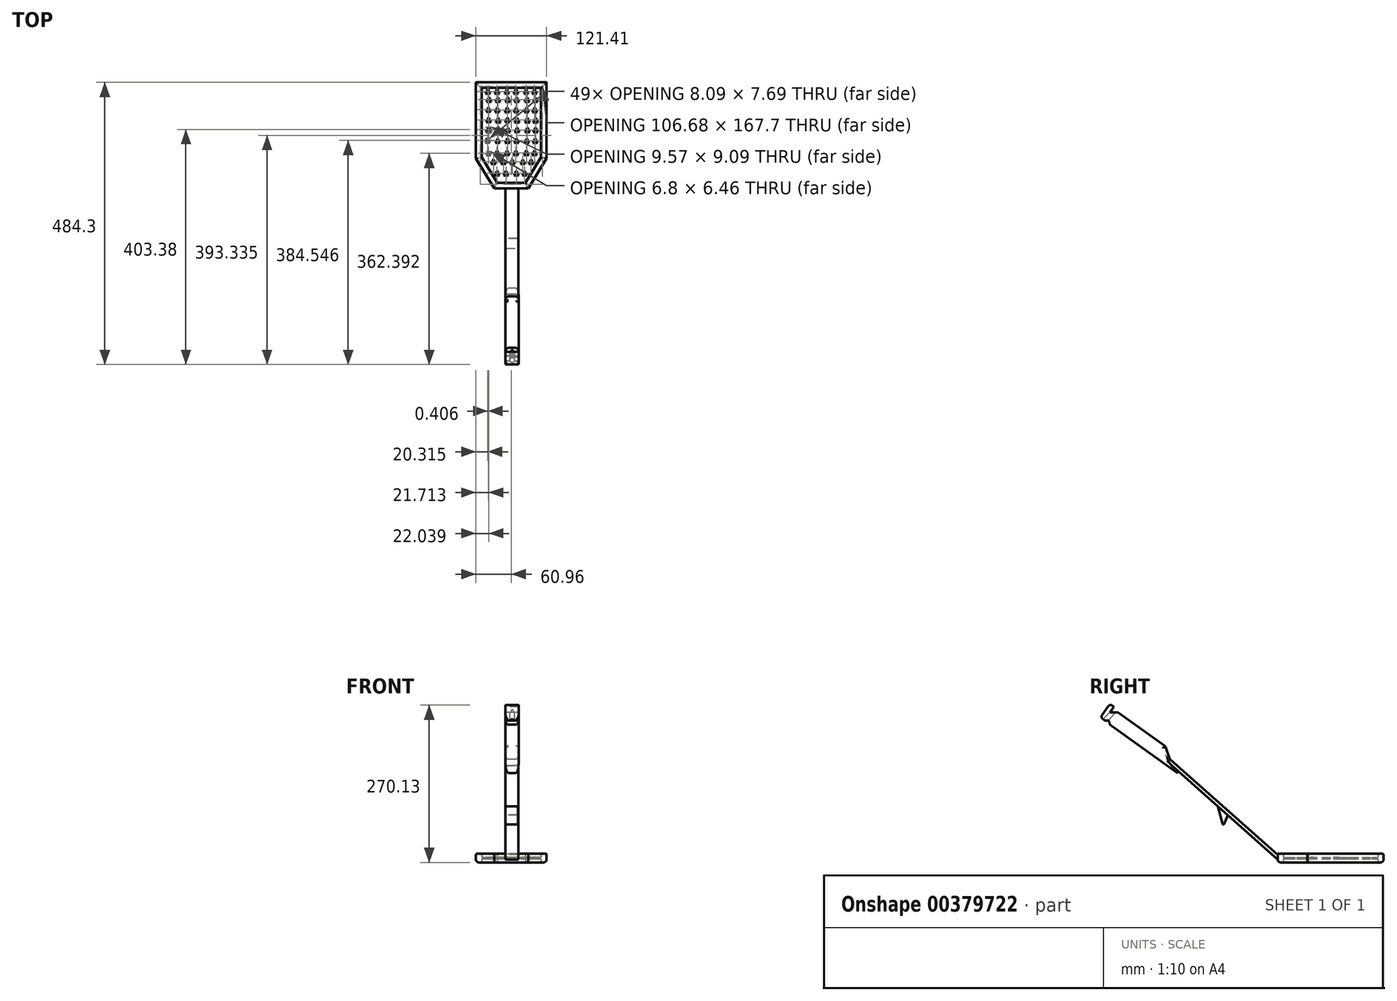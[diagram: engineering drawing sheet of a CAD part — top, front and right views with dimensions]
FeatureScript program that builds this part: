
annotation { "Feature Type Name" : "Feature", "Feature Type Description" : "" }
export const myFeature = defineFeature(function(context is Context, id is Id, definition is map)
    precondition{}
    {
        {
            var Q0;
            Q0=qCreatedBy(makeId("Top.planeOp"),FACE);
            var sketch = newSketch(context, id + "F0", { "sketchPlane" : qUnion([Q0])});
            skLineSegment(sketch, "E0", {"start": v(-14.17, -76.81) * mm, "end": v(34.1, -76.81) * mm});
            skLineSegment(sketch, "E1", {"start": v(-14.17, -76.81) * mm, "end": v(-40.84, -33.58) * mm});
            skLineSegment(sketch, "E2", {"start": v(-40.84, -33.58) * mm, "end": v(-40.84, 85.8) * mm});
            skLineSegment(sketch, "E3", {"start": v(-40.84, 85.8) * mm, "end": v(60.76, 85.8) * mm});
            skLineSegment(sketch, "E4", {"start": v(60.76, 85.8) * mm, "end": v(60.76, -33.58) * mm});
            skLineSegment(sketch, "E5", {"start": v(60.76, -33.58) * mm, "end": v(34.1, -76.81) * mm});
            skLineSegment(sketch, "E6", {"start": v(-51, 95.46) * mm, "end": v(70.41, 95.46) * mm});
            skLineSegment(sketch, "E7", {"start": v(70.41, 95.46) * mm, "end": v(70.41, -35.5) * mm});
            skLineSegment(sketch, "E8", {"start": v(70.41, -35.5) * mm, "end": v(38.97, -86.46) * mm});
            skLineSegment(sketch, "E9", {"start": v(38.97, -86.46) * mm, "end": v(-19.56, -86.46) * mm});
            skLineSegment(sketch, "E10", {"start": v(-19.56, -86.46) * mm, "end": v(-51, -35.5) * mm});
            skLineSegment(sketch, "E11", {"start": v(-51, -35.5) * mm, "end": v(-51, 95.46) * mm});
            skSolve(sketch);
        }
        {
            var Q0;
            Q0=makeQuery(id+"F0.imprint","IMPRINT",FACE,{"disambiguationData":[TD([[makeQuery(id+"F0.imprint","IMPRINT",EDGE,{"derivedFrom":sQuery(id+"F0.wireOp",EDGE,"E0")}),-1.0]])]});
            extrude(context, id + "F1", {"entities" : qUnion([Q0]), "depth" : 7.62 * mm});
        }
        {
            var Q0;
            Q0 = qSketchRegion(id + "F0", true);
            extrude(context, id + "F2", {"entities" : qUnion([Q0]), "operationType" : NewBodyOperationType.ADD, "oppositeDirection" : true, "depth" : 7.62 * mm});
        }
        {
            var Q0;
            Q0=qCreatedBy(makeId("Top.planeOp"),FACE);
            var sketch = newSketch(context, id + "F3", { "sketchPlane" : qUnion([Q0])});
            skLineSegment(sketch, "E12.0", {"start": v(-14.17, -76.81) * mm, "end": v(34.1, -76.81) * mm});
            skLineSegment(sketch, "E12.1", {"start": v(-14.17, -76.81) * mm, "end": v(-40.84, -33.58) * mm});
            skLineSegment(sketch, "E12.2", {"start": v(-40.84, -33.58) * mm, "end": v(-40.84, 85.8) * mm});
            skLineSegment(sketch, "E12.3", {"start": v(-40.84, 85.8) * mm, "end": v(60.76, 85.8) * mm});
            skLineSegment(sketch, "E12.4", {"start": v(60.76, 85.8) * mm, "end": v(60.76, -33.58) * mm});
            skLineSegment(sketch, "E12.5", {"start": v(60.76, -33.58) * mm, "end": v(34.1, -76.81) * mm});
            skLineSegment(sketch, "E12.6", {"start": v(70.41, 95.46) * mm, "end": v(70.41, -35.5) * mm});
            skLineSegment(sketch, "E12.7", {"start": v(70.41, -35.5) * mm, "end": v(38.97, -86.46) * mm});
            skLineSegment(sketch, "E12.8", {"start": v(38.97, -86.46) * mm, "end": v(-19.56, -86.46) * mm});
            skLineSegment(sketch, "E12.9", {"start": v(-19.56, -86.46) * mm, "end": v(-51, -35.5) * mm});
            skLineSegment(sketch, "E13.0", {"start": v(-51, 95.46) * mm, "end": v(70.41, 95.46) * mm});
            skLineSegment(sketch, "E13.1", {"start": v(-51, -35.5) * mm, "end": v(-51, 95.46) * mm});
            skLineSegment(sketch, "E13.6", {"start": v(-51, -35.5) * mm, "end": v(-51, 95.46) * mm});
            skLineSegment(sketch, "E13.9", {"start": v(-51, 95.46) * mm, "end": v(70.41, 95.46) * mm});
            skSolve(sketch);
        }
        {
            var Q0;
            Q0=qCreatedBy(makeId("Top.planeOp"),FACE);
            var sketch = newSketch(context, id + "F4", { "sketchPlane" : qUnion([Q0])});
            skLineSegment(sketch, "E14.0", {"start": v(-51, 95.46) * mm, "end": v(70.41, 95.46) * mm});
            skLineSegment(sketch, "E14.1", {"start": v(-51, 95.46) * mm, "end": v(70.41, 95.46) * mm});
            skLineSegment(sketch, "E15.0", {"start": v(70.41, 95.46) * mm, "end": v(70.41, -35.5) * mm});
            skLineSegment(sketch, "E15.1", {"start": v(70.41, 95.46) * mm, "end": v(70.41, -35.5) * mm});
            skLineSegment(sketch, "E16.0", {"start": v(-51, -35.5) * mm, "end": v(-51, 95.46) * mm});
            skLineSegment(sketch, "E16.1", {"start": v(-51, -35.5) * mm, "end": v(-51, 95.46) * mm});
            skPoint(sketch, "E17.0", {"position": v(-19.56, -86.46) * mm});
            skLineSegment(sketch, "E18.0", {"start": v(38.97, -86.46) * mm, "end": v(-19.56, -86.46) * mm});
            skLineSegment(sketch, "E18.1", {"start": v(38.97, -86.46) * mm, "end": v(-19.56, -86.46) * mm});
            skLineSegment(sketch, "E19", {"start": v(-51, -35.5) * mm, "end": v(-19.56, -86.46) * mm});
            skLineSegment(sketch, "E20", {"start": v(70.41, -35.5) * mm, "end": v(38.97, -86.46) * mm});
            skLineSegment(sketch, "E21.MirrorCS", {"start": v(-18.83, 76.12) * mm, "end": v(-14.78, 83.8) * mm});
            skLineSegment(sketch, "E22.MirrorCS", {"start": v(-14.78, 83.8) * mm, "end": v(-10.73, 76.12) * mm});
            skLineSegment(sketch, "E23.MirrorCS", {"start": v(-10.73, 76.12) * mm, "end": v(-18.83, 76.12) * mm});
            skLineSegment(sketch, "E24.MirrorCS", {"start": v(6.26, 76.12) * mm, "end": v(2.22, 83.8) * mm});
            skLineSegment(sketch, "E25.MirrorCS", {"start": v(13.54, 76.12) * mm, "end": v(17.6, 83.8) * mm});
            skLineSegment(sketch, "E26.MirrorCS", {"start": v(17.6, 83.8) * mm, "end": v(21.64, 76.12) * mm});
            skLineSegment(sketch, "E27.MirrorCS", {"start": v(-1.83, 76.12) * mm, "end": v(6.26, 76.12) * mm});
            skLineSegment(sketch, "E28.MirrorCS", {"start": v(2.22, 83.8) * mm, "end": v(-1.83, 76.12) * mm});
            skLineSegment(sketch, "E29.MirrorCS", {"start": v(21.64, 76.12) * mm, "end": v(13.54, 76.12) * mm});
            skLineSegment(sketch, "E30.MirrorCS", {"start": v(45.52, 76.12) * mm, "end": v(49.56, 83.8) * mm});
            skLineSegment(sketch, "E31.MirrorCS", {"start": v(35.4, 83.8) * mm, "end": v(31.35, 76.12) * mm});
            skLineSegment(sketch, "E32.MirrorCS", {"start": v(31.35, 76.12) * mm, "end": v(39.44, 76.12) * mm});
            skLineSegment(sketch, "E33.MirrorCS", {"start": v(53.6, 76.12) * mm, "end": v(45.52, 76.12) * mm});
            skLineSegment(sketch, "E34.MirrorCS", {"start": v(39.44, 76.12) * mm, "end": v(35.4, 83.8) * mm});
            skLineSegment(sketch, "E35.MirrorCS", {"start": v(49.56, 83.8) * mm, "end": v(53.6, 76.12) * mm});
            skLineSegment(sketch, "E36.MirrorCS", {"start": v(-17.21, 61.78) * mm, "end": v(-13.17, 69.47) * mm});
            skLineSegment(sketch, "E37.MirrorCS", {"start": v(-13.17, 69.47) * mm, "end": v(-9.12, 61.78) * mm});
            skLineSegment(sketch, "E38.MirrorCS", {"start": v(-9.12, 61.78) * mm, "end": v(-17.21, 61.78) * mm});
            skLineSegment(sketch, "E39.MirrorCS", {"start": v(7.87, 61.78) * mm, "end": v(3.83, 69.47) * mm});
            skLineSegment(sketch, "E40.MirrorCS", {"start": v(15.16, 61.78) * mm, "end": v(19.2, 69.47) * mm});
            skLineSegment(sketch, "E41.MirrorCS", {"start": v(19.2, 69.47) * mm, "end": v(23.25, 61.78) * mm});
            skLineSegment(sketch, "E42.MirrorCS", {"start": v(-0.22, 61.78) * mm, "end": v(7.87, 61.78) * mm});
            skLineSegment(sketch, "E43.MirrorCS", {"start": v(3.83, 69.47) * mm, "end": v(-0.22, 61.78) * mm});
            skLineSegment(sketch, "E44.MirrorCS", {"start": v(23.25, 61.78) * mm, "end": v(15.16, 61.78) * mm});
            skLineSegment(sketch, "E45.MirrorCS", {"start": v(47.13, 61.78) * mm, "end": v(51.17, 69.47) * mm});
            skLineSegment(sketch, "E46.MirrorCS", {"start": v(37, 69.47) * mm, "end": v(32.96, 61.78) * mm});
            skLineSegment(sketch, "E47.MirrorCS", {"start": v(32.96, 61.78) * mm, "end": v(41.05, 61.78) * mm});
            skLineSegment(sketch, "E48.MirrorCS", {"start": v(55.22, 61.78) * mm, "end": v(47.13, 61.78) * mm});
            skLineSegment(sketch, "E49.MirrorCS", {"start": v(41.05, 61.78) * mm, "end": v(37, 69.47) * mm});
            skLineSegment(sketch, "E50.MirrorCS", {"start": v(51.17, 69.47) * mm, "end": v(55.22, 61.78) * mm});
            skLineSegment(sketch, "E51.MirrorCS", {"start": v(-18.36, 44.38) * mm, "end": v(-14.28, 52.14) * mm});
            skLineSegment(sketch, "E52.MirrorCS", {"start": v(-14.28, 52.14) * mm, "end": v(-10.23, 44.46) * mm});
            skLineSegment(sketch, "E53.MirrorCS", {"start": v(-18.33, 44.46) * mm, "end": v(-14.28, 52.14) * mm});
            skLineSegment(sketch, "E54.MirrorCS", {"start": v(-10.23, 44.46) * mm, "end": v(-18.33, 44.46) * mm});
            skLineSegment(sketch, "E55.MirrorCS", {"start": v(6.76, 44.46) * mm, "end": v(2.72, 52.14) * mm});
            skLineSegment(sketch, "E56.MirrorCS", {"start": v(14.05, 44.46) * mm, "end": v(18.1, 52.14) * mm});
            skLineSegment(sketch, "E57.MirrorCS", {"start": v(18.1, 52.14) * mm, "end": v(22.14, 44.46) * mm});
            skLineSegment(sketch, "E58.MirrorCS", {"start": v(-1.33, 44.46) * mm, "end": v(6.76, 44.46) * mm});
            skLineSegment(sketch, "E59.MirrorCS", {"start": v(2.72, 52.14) * mm, "end": v(-1.33, 44.46) * mm});
            skLineSegment(sketch, "E60.MirrorCS", {"start": v(22.14, 44.46) * mm, "end": v(14.05, 44.46) * mm});
            skLineSegment(sketch, "E61.MirrorCS", {"start": v(46.02, 44.46) * mm, "end": v(50.06, 52.14) * mm});
            skLineSegment(sketch, "E62.MirrorCS", {"start": v(35.9, 52.14) * mm, "end": v(31.85, 44.46) * mm});
            skLineSegment(sketch, "E63.MirrorCS", {"start": v(31.85, 44.46) * mm, "end": v(39.94, 44.46) * mm});
            skLineSegment(sketch, "E64.MirrorCS", {"start": v(54.11, 44.46) * mm, "end": v(46.02, 44.46) * mm});
            skLineSegment(sketch, "E65.MirrorCS", {"start": v(39.94, 44.46) * mm, "end": v(35.9, 52.14) * mm});
            skLineSegment(sketch, "E66.MirrorCS", {"start": v(50.06, 52.14) * mm, "end": v(54.11, 44.46) * mm});
            skLineSegment(sketch, "E67.MirrorCS", {"start": v(-12.67, 34.42) * mm, "end": v(-8.62, 26.73) * mm});
            skLineSegment(sketch, "E68.MirrorCS", {"start": v(-16.71, 26.73) * mm, "end": v(-12.67, 34.42) * mm});
            skLineSegment(sketch, "E69.MirrorCS", {"start": v(-8.62, 26.73) * mm, "end": v(-16.71, 26.73) * mm});
            skLineSegment(sketch, "E70.MirrorCS", {"start": v(15.66, 26.73) * mm, "end": v(19.7, 34.42) * mm});
            skLineSegment(sketch, "E71.MirrorCS", {"start": v(19.7, 34.42) * mm, "end": v(23.75, 26.73) * mm});
            skLineSegment(sketch, "E72.MirrorCS", {"start": v(23.75, 26.73) * mm, "end": v(15.66, 26.73) * mm});
            skLineSegment(sketch, "E73.MirrorCS", {"start": v(47.63, 26.73) * mm, "end": v(51.68, 34.42) * mm});
            skLineSegment(sketch, "E74.MirrorCS", {"start": v(37.5, 34.42) * mm, "end": v(33.46, 26.73) * mm});
            skLineSegment(sketch, "E75.MirrorCS", {"start": v(33.46, 26.73) * mm, "end": v(41.55, 26.73) * mm});
            skLineSegment(sketch, "E76.MirrorCS", {"start": v(55.72, 26.73) * mm, "end": v(47.63, 26.73) * mm});
            skLineSegment(sketch, "E77.MirrorCS", {"start": v(41.55, 26.73) * mm, "end": v(37.5, 34.42) * mm});
            skLineSegment(sketch, "E78.MirrorCS", {"start": v(51.68, 34.42) * mm, "end": v(55.72, 26.73) * mm});
            skLineSegment(sketch, "E79", {"start": v(-33.75, 10) * mm, "end": v(-24.18, 10) * mm});
            skLineSegment(sketch, "E80", {"start": v(-24.18, 10) * mm, "end": v(-28.96, 19.09) * mm});
            skLineSegment(sketch, "E81", {"start": v(-28.96, 19.09) * mm, "end": v(-33.75, 10) * mm});
            skLineSegment(sketch, "E82.MirrorCS", {"start": v(-16.8, 9.8) * mm, "end": v(-12.75, 17.5) * mm});
            skLineSegment(sketch, "E83.MirrorCS", {"start": v(-12.75, 17.5) * mm, "end": v(-8.7, 9.8) * mm});
            skLineSegment(sketch, "E84.MirrorCS", {"start": v(-8.7, 9.8) * mm, "end": v(-16.8, 9.8) * mm});
            skLineSegment(sketch, "E85.MirrorCS", {"start": v(8.3, 9.8) * mm, "end": v(4.25, 17.5) * mm});
            skLineSegment(sketch, "E86.MirrorCS", {"start": v(15.58, 9.8) * mm, "end": v(19.62, 17.5) * mm});
            skLineSegment(sketch, "E87.MirrorCS", {"start": v(19.62, 17.5) * mm, "end": v(23.67, 9.8) * mm});
            skLineSegment(sketch, "E88.MirrorCS", {"start": v(0.2, 9.8) * mm, "end": v(8.3, 9.8) * mm});
            skLineSegment(sketch, "E89.MirrorCS", {"start": v(4.25, 17.5) * mm, "end": v(0.2, 9.8) * mm});
            skLineSegment(sketch, "E90.MirrorCS", {"start": v(23.67, 9.8) * mm, "end": v(15.58, 9.8) * mm});
            skLineSegment(sketch, "E91.MirrorCS", {"start": v(47.55, 9.8) * mm, "end": v(51.6, 17.5) * mm});
            skLineSegment(sketch, "E92.MirrorCS", {"start": v(37.43, 17.5) * mm, "end": v(33.38, 9.8) * mm});
            skLineSegment(sketch, "E93.MirrorCS", {"start": v(33.38, 9.8) * mm, "end": v(41.47, 9.8) * mm});
            skLineSegment(sketch, "E94.MirrorCS", {"start": v(55.64, 9.8) * mm, "end": v(47.55, 9.8) * mm});
            skLineSegment(sketch, "E95.MirrorCS", {"start": v(41.47, 9.8) * mm, "end": v(37.43, 17.5) * mm});
            skLineSegment(sketch, "E96.MirrorCS", {"start": v(51.6, 17.5) * mm, "end": v(55.64, 9.8) * mm});
            skLineSegment(sketch, "E97.MirrorCS", {"start": v(-17.6, -8.32) * mm, "end": v(-13.55, -0.63) * mm});
            skLineSegment(sketch, "E98.MirrorCS", {"start": v(-13.55, -0.63) * mm, "end": v(-9.5, -8.32) * mm});
            skLineSegment(sketch, "E99.MirrorCS", {"start": v(-9.5, -8.32) * mm, "end": v(-17.6, -8.32) * mm});
            skLineSegment(sketch, "E100.MirrorCS", {"start": v(7.49, -8.32) * mm, "end": v(3.44, -0.63) * mm});
            skLineSegment(sketch, "E101.MirrorCS", {"start": v(14.77, -8.32) * mm, "end": v(18.82, -0.63) * mm});
            skLineSegment(sketch, "E102.MirrorCS", {"start": v(18.82, -0.63) * mm, "end": v(22.86, -8.32) * mm});
            skLineSegment(sketch, "E103.MirrorCS", {"start": v(-0.6, -8.32) * mm, "end": v(7.49, -8.32) * mm});
            skLineSegment(sketch, "E104.MirrorCS", {"start": v(3.44, -0.63) * mm, "end": v(-0.6, -8.32) * mm});
            skLineSegment(sketch, "E105.MirrorCS", {"start": v(22.86, -8.32) * mm, "end": v(14.77, -8.32) * mm});
            skLineSegment(sketch, "E106.MirrorCS", {"start": v(46.74, -8.32) * mm, "end": v(50.79, -0.63) * mm});
            skLineSegment(sketch, "E107.MirrorCS", {"start": v(36.62, -0.63) * mm, "end": v(32.58, -8.32) * mm});
            skLineSegment(sketch, "E108.MirrorCS", {"start": v(32.58, -8.32) * mm, "end": v(40.67, -8.32) * mm});
            skLineSegment(sketch, "E109.MirrorCS", {"start": v(54.84, -8.32) * mm, "end": v(46.74, -8.32) * mm});
            skLineSegment(sketch, "E110.MirrorCS", {"start": v(40.67, -8.32) * mm, "end": v(36.62, -0.63) * mm});
            skLineSegment(sketch, "E111.MirrorCS", {"start": v(50.79, -0.63) * mm, "end": v(54.84, -8.32) * mm});
            skLineSegment(sketch, "E112", {"start": v(-32.69, -29.68) * mm, "end": v(-25.89, -29.68) * mm});
            skLineSegment(sketch, "E113", {"start": v(-25.89, -29.68) * mm, "end": v(-29.29, -23.22) * mm});
            skLineSegment(sketch, "E114", {"start": v(-29.29, -23.22) * mm, "end": v(-32.69, -29.68) * mm});
            skLineSegment(sketch, "E115.MirrorCS", {"start": v(-18.6, -29.68) * mm, "end": v(-14.56, -21.99) * mm});
            skLineSegment(sketch, "E116.MirrorCS", {"start": v(-14.56, -21.99) * mm, "end": v(-10.51, -29.68) * mm});
            skLineSegment(sketch, "E117.MirrorCS", {"start": v(-10.51, -29.68) * mm, "end": v(-18.6, -29.68) * mm});
            skLineSegment(sketch, "E118.MirrorCS", {"start": v(6.48, -29.68) * mm, "end": v(2.44, -21.99) * mm});
            skLineSegment(sketch, "E119.MirrorCS", {"start": v(13.77, -29.68) * mm, "end": v(17.81, -21.99) * mm});
            skLineSegment(sketch, "E120.MirrorCS", {"start": v(17.81, -21.99) * mm, "end": v(21.86, -29.68) * mm});
            skLineSegment(sketch, "E121.MirrorCS", {"start": v(-1.61, -29.68) * mm, "end": v(6.48, -29.68) * mm});
            skLineSegment(sketch, "E122.MirrorCS", {"start": v(2.44, -21.99) * mm, "end": v(-1.61, -29.68) * mm});
            skLineSegment(sketch, "E123.MirrorCS", {"start": v(21.86, -29.68) * mm, "end": v(13.77, -29.68) * mm});
            skLineSegment(sketch, "E124.MirrorCS", {"start": v(45.74, -29.68) * mm, "end": v(49.78, -21.99) * mm});
            skLineSegment(sketch, "E125.MirrorCS", {"start": v(35.62, -21.99) * mm, "end": v(31.57, -29.68) * mm});
            skLineSegment(sketch, "E126.MirrorCS", {"start": v(31.57, -29.68) * mm, "end": v(39.66, -29.68) * mm});
            skLineSegment(sketch, "E127.MirrorCS", {"start": v(53.83, -29.68) * mm, "end": v(45.74, -29.68) * mm});
            skLineSegment(sketch, "E128.MirrorCS", {"start": v(39.66, -29.68) * mm, "end": v(35.62, -21.99) * mm});
            skLineSegment(sketch, "E129.MirrorCS", {"start": v(49.78, -21.99) * mm, "end": v(53.83, -29.68) * mm});
            skLineSegment(sketch, "E130.MirrorCS", {"start": v(-24.7, -44.99) * mm, "end": v(-20.66, -37.3) * mm});
            skLineSegment(sketch, "E131.MirrorCS", {"start": v(-20.66, -37.3) * mm, "end": v(-16.6, -44.99) * mm});
            skLineSegment(sketch, "E132.MirrorCS", {"start": v(-16.6, -44.99) * mm, "end": v(-24.7, -44.99) * mm});
            skLineSegment(sketch, "E133.MirrorCS", {"start": v(0.39, -44.99) * mm, "end": v(-3.66, -37.3) * mm});
            skLineSegment(sketch, "E134.MirrorCS", {"start": v(7.67, -44.99) * mm, "end": v(11.72, -37.3) * mm});
            skLineSegment(sketch, "E135.MirrorCS", {"start": v(11.72, -37.3) * mm, "end": v(15.76, -44.99) * mm});
            skLineSegment(sketch, "E136.MirrorCS", {"start": v(-7.7, -44.99) * mm, "end": v(0.39, -44.99) * mm});
            skLineSegment(sketch, "E137.MirrorCS", {"start": v(-3.66, -37.3) * mm, "end": v(-7.7, -44.99) * mm});
            skLineSegment(sketch, "E138.MirrorCS", {"start": v(15.76, -44.99) * mm, "end": v(7.67, -44.99) * mm});
            skLineSegment(sketch, "E139.MirrorCS", {"start": v(39.64, -44.99) * mm, "end": v(43.69, -37.3) * mm});
            skLineSegment(sketch, "E140.MirrorCS", {"start": v(29.52, -37.3) * mm, "end": v(25.47, -44.99) * mm});
            skLineSegment(sketch, "E141.MirrorCS", {"start": v(25.47, -44.99) * mm, "end": v(33.57, -44.99) * mm});
            skLineSegment(sketch, "E142.MirrorCS", {"start": v(47.73, -44.99) * mm, "end": v(39.64, -44.99) * mm});
            skLineSegment(sketch, "E143.MirrorCS", {"start": v(33.57, -44.99) * mm, "end": v(29.52, -37.3) * mm});
            skLineSegment(sketch, "E144.MirrorCS", {"start": v(43.69, -37.3) * mm, "end": v(47.73, -44.99) * mm});
            skLineSegment(sketch, "E145.MirrorCS", {"start": v(-10.54, -64.32) * mm, "end": v(-14.58, -56.64) * mm});
            skLineSegment(sketch, "E146.MirrorCS", {"start": v(-3.25, -64.32) * mm, "end": v(0.8, -56.64) * mm});
            skLineSegment(sketch, "E147.MirrorCS", {"start": v(0.8, -56.64) * mm, "end": v(4.84, -64.32) * mm});
            skLineSegment(sketch, "E148.MirrorCS", {"start": v(-18.63, -64.32) * mm, "end": v(-10.54, -64.32) * mm});
            skLineSegment(sketch, "E149.MirrorCS", {"start": v(-14.58, -56.64) * mm, "end": v(-18.63, -64.32) * mm});
            skLineSegment(sketch, "E150.MirrorCS", {"start": v(4.84, -64.32) * mm, "end": v(-3.25, -64.32) * mm});
            skLineSegment(sketch, "E151.MirrorCS", {"start": v(28.72, -64.32) * mm, "end": v(32.77, -56.64) * mm});
            skLineSegment(sketch, "E152.MirrorCS", {"start": v(18.6, -56.64) * mm, "end": v(14.55, -64.32) * mm});
            skLineSegment(sketch, "E153.MirrorCS", {"start": v(14.55, -64.32) * mm, "end": v(22.64, -64.32) * mm});
            skLineSegment(sketch, "E154.MirrorCS", {"start": v(36.81, -64.32) * mm, "end": v(28.72, -64.32) * mm});
            skLineSegment(sketch, "E155.MirrorCS", {"start": v(22.64, -64.32) * mm, "end": v(18.6, -56.64) * mm});
            skLineSegment(sketch, "E156.MirrorCS", {"start": v(32.77, -56.64) * mm, "end": v(36.81, -64.32) * mm});
            skLineSegment(sketch, "E157.MirrorCS", {"start": v(-34.33, 75.74) * mm, "end": v(-30.28, 83.43) * mm});
            skLineSegment(sketch, "E158.MirrorCS", {"start": v(-30.28, 83.43) * mm, "end": v(-26.23, 75.74) * mm});
            skLineSegment(sketch, "E159.MirrorCS", {"start": v(-26.23, 75.74) * mm, "end": v(-34.33, 75.74) * mm});
            skLineSegment(sketch, "E160.MirrorCS", {"start": v(-32.71, 62.05) * mm, "end": v(-28.67, 69.73) * mm});
            skLineSegment(sketch, "E161.MirrorCS", {"start": v(-28.67, 69.73) * mm, "end": v(-24.62, 62.05) * mm});
            skLineSegment(sketch, "E162.MirrorCS", {"start": v(-24.62, 62.05) * mm, "end": v(-32.71, 62.05) * mm});
            skLineSegment(sketch, "E163.MirrorCS", {"start": v(-33.52, 44.72) * mm, "end": v(-29.47, 52.4) * mm});
            skLineSegment(sketch, "E164.MirrorCS", {"start": v(-29.47, 52.4) * mm, "end": v(-25.43, 44.72) * mm});
            skLineSegment(sketch, "E165.MirrorCS", {"start": v(-25.43, 44.72) * mm, "end": v(-33.52, 44.72) * mm});
            skLineSegment(sketch, "E166.MirrorCS", {"start": v(-33.12, 26.96) * mm, "end": v(-29.07, 34.65) * mm});
            skLineSegment(sketch, "E167.MirrorCS", {"start": v(-29.07, 34.65) * mm, "end": v(-25.02, 26.96) * mm});
            skLineSegment(sketch, "E168.MirrorCS", {"start": v(-25.02, 26.96) * mm, "end": v(-33.12, 26.96) * mm});
            skLineSegment(sketch, "E169.MirrorCS", {"start": v(-34.73, -8.14) * mm, "end": v(-30.69, -0.45) * mm});
            skLineSegment(sketch, "E170.MirrorCS", {"start": v(-30.69, -0.45) * mm, "end": v(-26.64, -8.14) * mm});
            skLineSegment(sketch, "E171.MirrorCS", {"start": v(-26.64, -8.14) * mm, "end": v(-34.73, -8.14) * mm});
            skLineSegment(sketch, "E172.MirrorCS", {"start": v(-0.87, 27) * mm, "end": v(3.17, 34.7) * mm});
            skLineSegment(sketch, "E173.MirrorCS", {"start": v(3.17, 34.7) * mm, "end": v(7.22, 27) * mm});
            skLineSegment(sketch, "E174.MirrorCS", {"start": v(7.22, 27) * mm, "end": v(-0.87, 27) * mm});
            skSolve(sketch);
        }
        {
            var Q0;
            Q0=makeQuery(id+"F1.opExtrude","CAP_EDGE",EDGE,{"disambiguationData":[OSD([sQuery(id+"F0.wireOp",EDGE,"E5")])],"isStart":false});
            var Q1;
            Q1=makeQuery(id+"F1.opExtrude","CAP_EDGE",EDGE,{"disambiguationData":[OSD([sQuery(id+"F0.wireOp",EDGE,"E0")])],"isStart":false});
            var Q2;
            Q2=makeQuery(id+"F1.opExtrude","CAP_EDGE",EDGE,{"disambiguationData":[OSD([sQuery(id+"F0.wireOp",EDGE,"E1")])],"isStart":false});
            var Q3;
            Q3=makeQuery(id+"F1.opExtrude","CAP_EDGE",EDGE,{"disambiguationData":[OSD([sQuery(id+"F0.wireOp",EDGE,"E2")])],"isStart":false});
            var Q4;
            Q4=makeQuery(id+"F1.opExtrude","CAP_EDGE",EDGE,{"disambiguationData":[OSD([sQuery(id+"F0.wireOp",EDGE,"E3")])],"isStart":false});
            var Q5;
            Q5=makeQuery(id+"F1.opExtrude","CAP_EDGE",EDGE,{"disambiguationData":[OSD([sQuery(id+"F0.wireOp",EDGE,"E4")])],"isStart":false});
            var Q6;
            Q6=makeQuery(id+"F1.opExtrude","CAP_EDGE",EDGE,{"disambiguationData":[OSD([sQuery(id+"F0.wireOp",EDGE,"E8")])],"isStart":false});
            var Q7;
            Q7=makeQuery(id+"F1.opExtrude","CAP_EDGE",EDGE,{"disambiguationData":[OSD([sQuery(id+"F0.wireOp",EDGE,"E9")])],"isStart":false});
            var Q8;
            Q8=makeQuery(id+"F1.opExtrude","CAP_EDGE",EDGE,{"disambiguationData":[OSD([sQuery(id+"F0.wireOp",EDGE,"E10")])],"isStart":false});
            var Q9;
            Q9=makeQuery(id+"F1.opExtrude","CAP_EDGE",EDGE,{"disambiguationData":[OSD([sQuery(id+"F0.wireOp",EDGE,"E11")])],"isStart":false});
            var Q10;
            Q10=makeQuery(id+"F1.opExtrude","CAP_EDGE",EDGE,{"disambiguationData":[OSD([sQuery(id+"F0.wireOp",EDGE,"E7")])],"isStart":false});
            var Q11;
            Q11=makeQuery(id+"F1.opExtrude","CAP_EDGE",EDGE,{"disambiguationData":[OSD([sQuery(id+"F0.wireOp",EDGE,"E6")])],"isStart":false});
            var Q12;
            Q12=makeQuery(id+"F2.opExtrude","CAP_EDGE",EDGE,{"disambiguationData":[OSD([sQuery(id+"F0.wireOp",EDGE,"E5")])],"isStart":false});
            var Q13;
            Q13=makeQuery(id+"F2.opExtrude","CAP_EDGE",EDGE,{"disambiguationData":[OSD([sQuery(id+"F0.wireOp",EDGE,"E0")])],"isStart":false});
            var Q14;
            Q14=makeQuery(id+"F2.opExtrude","CAP_EDGE",EDGE,{"disambiguationData":[OSD([sQuery(id+"F0.wireOp",EDGE,"E1")])],"isStart":false});
            var Q15;
            Q15=makeQuery(id+"F2.opExtrude","CAP_EDGE",EDGE,{"disambiguationData":[OSD([sQuery(id+"F0.wireOp",EDGE,"E2")])],"isStart":false});
            var Q16;
            Q16=makeQuery(id+"F2.opExtrude","CAP_EDGE",EDGE,{"disambiguationData":[OSD([sQuery(id+"F0.wireOp",EDGE,"E3")])],"isStart":false});
            var Q17;
            Q17=makeQuery(id+"F2.opExtrude","CAP_EDGE",EDGE,{"disambiguationData":[OSD([sQuery(id+"F0.wireOp",EDGE,"E4")])],"isStart":false});
            fillet(context, id + "F5", {"entities" : qUnion([Q0, Q1, Q2, Q3, Q4, Q5, Q6, Q7, Q8, Q9, Q10, Q11, Q12, Q13, Q14, Q15, Q16, Q17]), "radius" : 2.54 * mm, "tangentPropagation" : true, "allowEdgeOverflow" : false});
        }
        {
            var Q0;
            Q0=makeQuery(id+"F2.opExtrude","CAP_EDGE",EDGE,{"disambiguationData":[OSD([sQuery(id+"F0.wireOp",EDGE,"E7")])],"isStart":false});
            var Q1;
            Q1=makeQuery(id+"F2.opExtrude","CAP_EDGE",EDGE,{"disambiguationData":[OSD([sQuery(id+"F0.wireOp",EDGE,"E6")])],"isStart":false});
            var Q2;
            Q2=makeQuery(id+"F2.opExtrude","CAP_EDGE",EDGE,{"disambiguationData":[OSD([sQuery(id+"F0.wireOp",EDGE,"E11")])],"isStart":false});
            var Q3;
            Q3=makeQuery(id+"F2.opExtrude","CAP_EDGE",EDGE,{"disambiguationData":[OSD([sQuery(id+"F0.wireOp",EDGE,"E10")])],"isStart":false});
            var Q4;
            Q4=makeQuery(id+"F2.opExtrude","CAP_EDGE",EDGE,{"disambiguationData":[OSD([sQuery(id+"F0.wireOp",EDGE,"E9")])],"isStart":false});
            var Q5;
            Q5=makeQuery(id+"F2.opExtrude","CAP_EDGE",EDGE,{"disambiguationData":[OSD([sQuery(id+"F0.wireOp",EDGE,"E8")])],"isStart":false});
            fillet(context, id + "F6", {"entities" : qUnion([Q0, Q1, Q2, Q3, Q4, Q5]), "radius" : 5.08 * mm, "tangentPropagation" : true, "allowEdgeOverflow" : false});
        }
        {
            var Q0;
            Q0 = qSketchRegion(id + "F4", true);
            extrude(context, id + "F7", {"entities" : qUnion([Q0]), "operationType" : NewBodyOperationType.ADD, "endBound" : BoundingType.SYMMETRIC, "oppositeDirection" : true, "depth" : 2.54 * mm});
        }
        {
            var Q0;
            Q0=qCreatedBy(makeId("Right.planeOp"),FACE);
            var sketch = newSketch(context, id + "F8", { "sketchPlane" : qUnion([Q0])});
            skLineSegment(sketch, "E175", {"start": v(-86.15, 5) * mm, "end": v(-352.18, 240.96) * mm});
            skLineSegment(sketch, "E176", {"start": v(-86.54, -2.51) * mm, "end": v(-351.67, 232.64) * mm});
            skLineSegment(sketch, "E177", {"start": v(-351.67, 232.64) * mm, "end": v(-356.05, 236.58) * mm});
            skLineSegment(sketch, "E178", {"start": v(-356.05, 236.58) * mm, "end": v(-352.18, 240.96) * mm});
            skLineSegment(sketch, "E179", {"start": v(-86.15, 5) * mm, "end": v(-86.54, -2.51) * mm});
            skSolve(sketch);
        }
        {
            var Q0;
            Q0=makeQuery(id+"F8.imprint","IMPRINT",FACE,{"disambiguationData":[TD([[makeQuery(id+"F8.imprint","IMPRINT",EDGE,{"derivedFrom":sQuery(id+"F8.wireOp",EDGE,"E175")}),1.0]])]});
            extrude(context, id + "F9", {"entities" : qUnion([Q0]), "operationType" : NewBodyOperationType.ADD, "depth" : 21.84 * mm});
        }
        {
            var Q0;
            Q0=qCreatedBy(makeId("Right.planeOp"),FACE);
            var sketch = newSketch(context, id + "F10", { "sketchPlane" : qUnion([Q0])});
            skLineSegment(sketch, "E180", {"start": v(-268.32, 158.61) * mm, "end": v(-258.08, 146.04) * mm});
            skLineSegment(sketch, "E181", {"start": v(-258.08, 146.04) * mm, "end": v(-374.2, 229.1) * mm});
            skLineSegment(sketch, "E182", {"start": v(-374.2, 229.1) * mm, "end": v(-376.53, 236.11) * mm});
            skLineSegment(sketch, "E183", {"start": v(-376.53, 236.11) * mm, "end": v(-383.26, 236.11) * mm});
            skLineSegment(sketch, "E184", {"start": v(-383.26, 236.11) * mm, "end": v(-390.86, 241.67) * mm});
            skLineSegment(sketch, "E185", {"start": v(-390.86, 241.67) * mm, "end": v(-374.2, 264.48) * mm});
            skLineSegment(sketch, "E186", {"start": v(-374.2, 264.48) * mm, "end": v(-367.24, 259.5) * mm});
            skLineSegment(sketch, "E187", {"start": v(-367.24, 259.5) * mm, "end": v(-374.2, 249.79) * mm});
            skLineSegment(sketch, "E188", {"start": v(-374.2, 249.79) * mm, "end": v(-360.28, 249.79) * mm});
            skLineSegment(sketch, "E189", {"start": v(-360.28, 249.79) * mm, "end": v(-279.04, 191.67) * mm});
            skLineSegment(sketch, "E190", {"start": v(-279.04, 191.67) * mm, "end": v(-268.32, 158.61) * mm});
            skSolve(sketch);
        }
        {
            var Q0;
            Q0=makeQuery(id+"F10.imprint","IMPRINT",FACE,{"disambiguationData":[TD([[makeQuery(id+"F10.imprint","IMPRINT",EDGE,{"derivedFrom":sQuery(id+"F10.wireOp",EDGE,"E180")}),-1.0]])]});
            extrude(context, id + "F11", {"entities" : qUnion([Q0]), "operationType" : NewBodyOperationType.ADD, "depth" : 22.35 * mm});
        }
        {
            var Q0;
            Q0=makeQuery(id+"F11.opExtrude","CAP_EDGE",EDGE,{"disambiguationData":[OSD([sQuery(id+"F10.wireOp",EDGE,"E189")])],"isStart":false});
            var Q1;
            Q1=makeQuery(id+"F11.opExtrude","CAP_EDGE",EDGE,{"disambiguationData":[OSD([sQuery(id+"F10.wireOp",EDGE,"E189")])],"isStart":true});
            var Q2;
            {var subQ0=sQuery(id+"F8.wireOp",EDGE,"E175");var subQ2=sQuery(id+"F10.wireOp",EDGE,"E190");Q2=makeQuery(id+"F11.boolean.opBoolean","SPLIT",EDGE,{"disambiguationData":[TD([makeQuery(id+"F9.opExtrude","SWEPT_FACE",FACE,{"disambiguationData":[OSD([subQ0])]})])],"derivedFrom":makeQuery(id+"F11.opExtrude","CAP_EDGE",EDGE,{"disambiguationData":[OSD([subQ2])],"isStart":true})});}
            var Q3;
            Q3=makeQuery(id+"F11.opExtrude","CAP_EDGE",EDGE,{"disambiguationData":[OSD([sQuery(id+"F10.wireOp",EDGE,"E181")])],"isStart":false});
            fillet(context, id + "F12", {"entities" : qUnion([Q0, Q1, Q2, Q3]), "radius" : 5.08 * mm, "tangentPropagation" : true, "allowEdgeOverflow" : false});
        }
        {
            var Q0;
            Q0=makeQuery(id+"F11.opExtrude","CAP_EDGE",EDGE,{"disambiguationData":[OSD([sQuery(id+"F10.wireOp",EDGE,"E181")])],"isStart":true});
            var Q1;
            Q1=makeQuery(id+"F11.opExtrude","SWEPT_EDGE",EDGE,{"disambiguationData":[OSD([sQuery(id+"F10.wireOp",EDGE,"E184"),sQuery(id+"F10.wireOp",EDGE,"E185")])]});
            var Q2;
            Q2=makeQuery(id+"F11.opExtrude","SWEPT_EDGE",EDGE,{"disambiguationData":[OSD([sQuery(id+"F10.wireOp",EDGE,"E185"),sQuery(id+"F10.wireOp",EDGE,"E186")])]});
            var Q3;
            Q3=makeQuery(id+"F11.opExtrude","CAP_EDGE",EDGE,{"disambiguationData":[OSD([sQuery(id+"F10.wireOp",EDGE,"E190")])],"isStart":false});
            fillet(context, id + "F13", {"entities" : qUnion([Q0, Q1, Q2, Q3]), "radius" : 5.08 * mm, "tangentPropagation" : true, "allowEdgeOverflow" : false});
        }
        {
            var Q0;
            Q0=qCreatedBy(makeId("Right.planeOp"),FACE);
            var sketch = newSketch(context, id + "F14", { "sketchPlane" : qUnion([Q0])});
            skLineSegment(sketch, "E191", {"start": v(-189.84, 90.54) * mm, "end": v(-179.88, 54.9) * mm});
            skLineSegment(sketch, "E192", {"start": v(-179.88, 54.9) * mm, "end": v(-172.06, 73.28) * mm});
            skLineSegment(sketch, "E193", {"start": v(-172.06, 73.28) * mm, "end": v(-189.84, 90.54) * mm});
            skSolve(sketch);
        }
        {
            var Q0;
            Q0=makeQuery(id+"F14.imprint","IMPRINT",FACE,{"disambiguationData":[TD([[makeQuery(id+"F14.imprint","IMPRINT",EDGE,{"derivedFrom":sQuery(id+"F14.wireOp",EDGE,"E191")}),1.0]])]});
            extrude(context, id + "F15", {"entities" : qUnion([Q0]), "operationType" : NewBodyOperationType.ADD, "depth" : 21.34 * mm});
        }
        {
            var Q0;
            Q0=makeQuery(id+"F15.opExtrude","SWEPT_EDGE",EDGE,{"disambiguationData":[OSD([sQuery(id+"F14.wireOp",EDGE,"E191"),sQuery(id+"F14.wireOp",EDGE,"E192")])]});
            var Q1;
            Q1=makeQuery(id+"F15.opExtrude","CAP_EDGE",EDGE,{"disambiguationData":[OSD([sQuery(id+"F14.wireOp",EDGE,"E191")])],"isStart":false});
            var Q2;
            Q2=makeQuery(id+"F15.opExtrude","CAP_EDGE",EDGE,{"disambiguationData":[OSD([sQuery(id+"F14.wireOp",EDGE,"E192")])],"isStart":true});
            var Q3;
            Q3=makeQuery(id+"F15.opExtrude","CAP_EDGE",EDGE,{"disambiguationData":[OSD([sQuery(id+"F14.wireOp",EDGE,"E192")])],"isStart":false});
            var Q4;
            Q4=makeQuery(id+"F15.opExtrude","CAP_EDGE",EDGE,{"disambiguationData":[OSD([sQuery(id+"F14.wireOp",EDGE,"E191")])],"isStart":true});
            fillet(context, id + "F16", {"entities" : qUnion([Q0, Q1, Q2, Q3, Q4]), "radius" : 1.27 * mm, "tangentPropagation" : true, "allowEdgeOverflow" : false});
        }
        {
            var Q0;
            Q0=makeQuery(id+"F9.opExtrude","SWEPT_FACE",FACE,{"disambiguationData":[OSD([sQuery(id+"F8.wireOp",EDGE,"E175")])]});
            cPlane(context, id + "F17", {"entities" : qUnion([Q0]), "cplaneType" : CPlaneType.OFFSET, "offset" : 68.58 * mm, "width" : 152.4 * mm, "height" : 152.4 * mm});
        }
        {
            var Q0;
            Q0=qCreatedBy(id+"F17.planeOp",FACE);
            var sketch = newSketch(context, id + "F18", { "sketchPlane" : qUnion([Q0])});
            skCircle(sketch, "E194", {"center": v(11.47, -442.5) * mm, "radius": 3.87 * mm});
            skSolve(sketch);
        }
        {
            var Q0;
            Q0=makeQuery(id+"F18.imprint","IMPRINT",FACE,{"disambiguationData":[TD([[makeQuery(id+"F18.imprint","IMPRINT",EDGE,{"derivedFrom":sQuery(id+"F18.wireOp",EDGE,"E194")}),1.0]])]});
            extrude(context, id + "F19", {"entities" : qUnion([Q0]), "operationType" : NewBodyOperationType.REMOVE, "oppositeDirection" : true, "depth" : 106.93 * mm});
        }
    });
